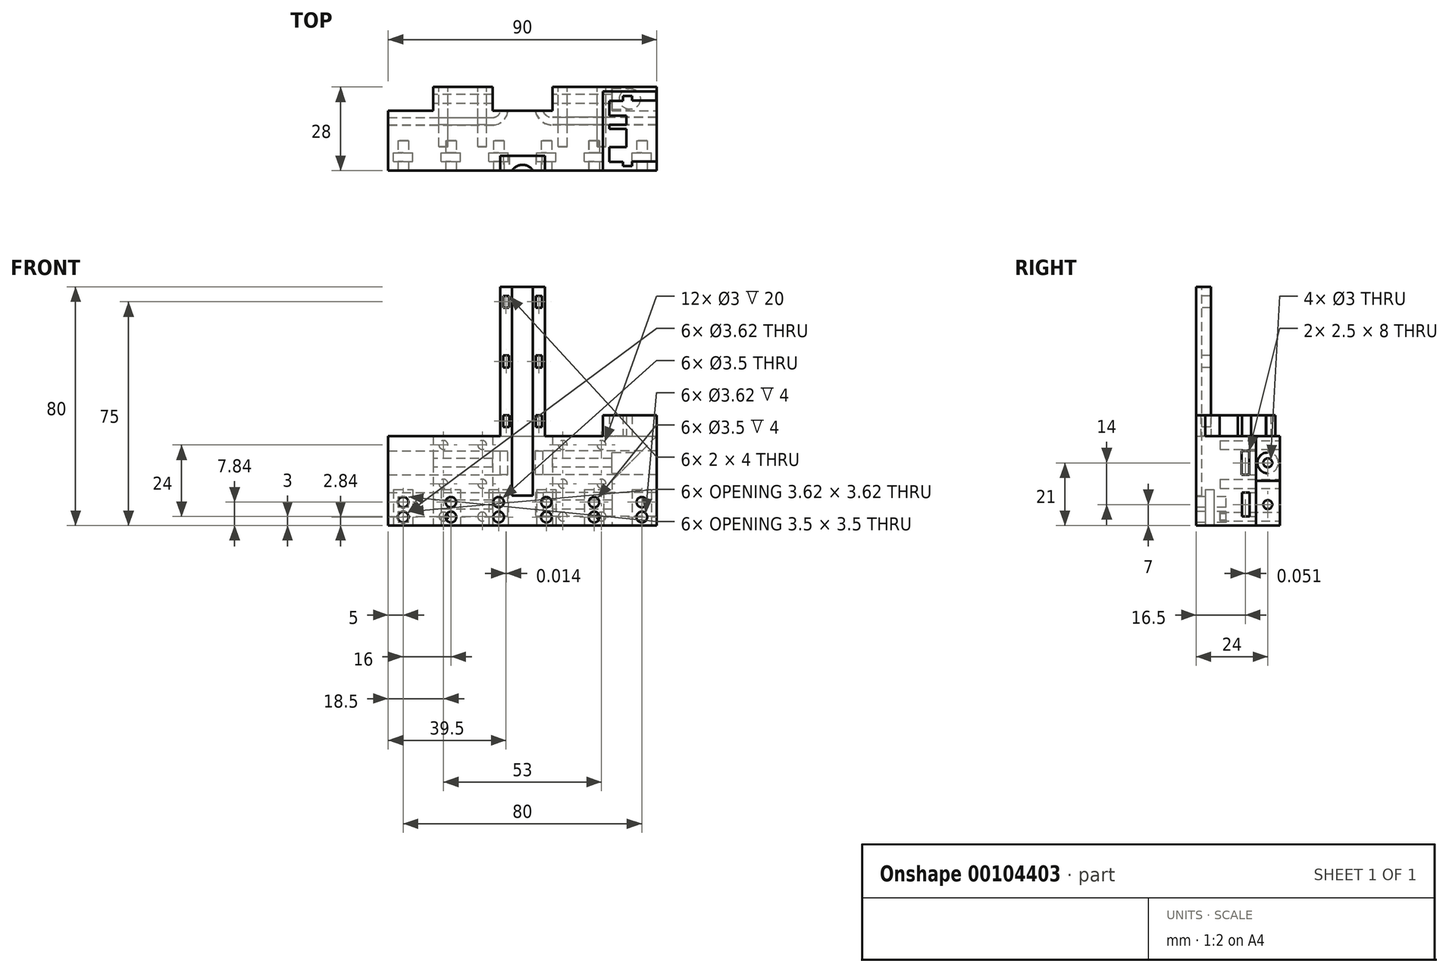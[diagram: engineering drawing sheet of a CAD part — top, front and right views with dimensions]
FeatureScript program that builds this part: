
annotation { "Feature Type Name" : "Feature", "Feature Type Description" : "" }
export const myFeature = defineFeature(function(context is Context, id is Id, definition is map)
    precondition{}
    {
        {
            var Q0;
            Q0=qCreatedBy(makeId("Top.planeOp"),FACE);
            var sketch = newSketch(context, id + "F0", { "sketchPlane" : qUnion([Q0])});
            skLineSegment(sketch, "E0.bottom", {"start": v(0, 0) * mm, "end": v(90, 0) * mm});
            skLineSegment(sketch, "E0.top", {"start": v(0, 20) * mm, "end": v(15, 20) * mm});
            skLineSegment(sketch, "E0.left", {"start": v(0, 0) * mm, "end": v(0, 20) * mm});
            skLineSegment(sketch, "E0.right", {"start": v(90, 0) * mm, "end": v(90, 20) * mm});
            skLineSegment(sketch, "E1.top", {"start": v(15, 28) * mm, "end": v(35, 28) * mm});
            skLineSegment(sketch, "E1.left", {"start": v(15, 20) * mm, "end": v(15, 28) * mm});
            skLineSegment(sketch, "E1.right", {"start": v(75, 20) * mm, "end": v(75, 28) * mm});
            skLineSegment(sketch, "E2.trimOffspring", {"start": v(75, 20) * mm, "end": v(90, 20) * mm});
            skLineSegment(sketch, "E3.top", {"start": v(35, 20) * mm, "end": v(55, 20) * mm});
            skLineSegment(sketch, "E3.left", {"start": v(35, 28) * mm, "end": v(35, 20) * mm});
            skLineSegment(sketch, "E3.right", {"start": v(55, 28) * mm, "end": v(55, 20) * mm});
            skLineSegment(sketch, "E4.trimOffspring", {"start": v(55, 28) * mm, "end": v(75, 28) * mm});
            skSolve(sketch);
        }
        {
            var Q0;
            Q0 = qSketchRegion(id + "F0", true);
            extrude(context, id + "F1", {"entities" : qUnion([Q0]), "depth" : 30 * mm});
        }
        {
            var Q0;
            Q0=makeQuery(id+"F1.opExtrude","CAP_FACE",FACE,{"disambiguationData":[OSD([sQuery(id+"F0.wireOp",EDGE,"E0.bottom"),sQuery(id+"F0.wireOp",EDGE,"E0.top"),sQuery(id+"F0.wireOp",EDGE,"E0.left"),sQuery(id+"F0.wireOp",EDGE,"E0.right"),sQuery(id+"F0.wireOp",EDGE,"E1.top"),sQuery(id+"F0.wireOp",EDGE,"E1.left"),sQuery(id+"F0.wireOp",EDGE,"E1.right"),sQuery(id+"F0.wireOp",EDGE,"E2.trimOffspring")])],"isStart":false});
            var sketch = newSketch(context, id + "F2", { "sketchPlane" : qUnion([Q0])});
            skLineSegment(sketch, "E5", {"start": v(0, 16.5) * mm, "end": v(35, 16.5) * mm});
            skArc(sketch, "E6", {"start": v(35, 16.5) * mm, "mid": v(37.78, 17.68) * mm, "end": v(38.86, 20.5) * mm});
            skLineSegment(sketch, "E7", {"start": v(90, 16.5) * mm, "end": v(55, 16.5) * mm});
            skArc(sketch, "E8", {"start": v(55, 16.5) * mm, "mid": v(51.9, 17.7) * mm, "end": v(50.38, 20.65) * mm});
            skSolve(sketch);
        }
        {
            var Q0;
            Q0=makeQuery(id+"F1.opExtrude","SWEPT_FACE",FACE,{"disambiguationData":[OSD([sQuery(id+"F0.wireOp",EDGE,"E0.left")])]});
            var sketch = newSketch(context, id + "F3", { "sketchPlane" : qUnion([Q0])});
            skLineSegment(sketch, "E9.bottom", {"start": v(-17.75, 25) * mm, "end": v(-15.25, 25) * mm});
            skLineSegment(sketch, "E9.top", {"start": v(-17.75, 17) * mm, "end": v(-15.25, 17) * mm});
            skLineSegment(sketch, "E9.left", {"start": v(-17.75, 25) * mm, "end": v(-17.75, 17) * mm});
            skLineSegment(sketch, "E9.right", {"start": v(-15.25, 25) * mm, "end": v(-15.25, 17) * mm});
            skLineSegment(sketch, "E10.bottom", {"start": v(-17.8, 11) * mm, "end": v(-15.3, 11) * mm});
            skLineSegment(sketch, "E10.top", {"start": v(-17.8, 3) * mm, "end": v(-15.3, 3) * mm});
            skLineSegment(sketch, "E10.left", {"start": v(-17.8, 11) * mm, "end": v(-17.8, 3) * mm});
            skLineSegment(sketch, "E10.right", {"start": v(-15.3, 11) * mm, "end": v(-15.3, 3) * mm});
            skSolve(sketch);
        }
        {
            var Q0;
            Q0 = qSketchRegion(id + "F3", true);
            var Q1;
            Q1=sQuery(id+"F2.wireOp",EDGE,"E5");
            var Q2;
            Q2=sQuery(id+"F2.wireOp",EDGE,"E6");
            sweep(context, id + "F4", {"operationType" : NewBodyOperationType.REMOVE, "profiles" : qUnion([Q0]), "path" : qUnion([Q1, Q2])});
        }
        {
            var Q0;
            Q0=makeQuery(id+"F1.opExtrude","SWEPT_FACE",FACE,{"disambiguationData":[OSD([sQuery(id+"F0.wireOp",EDGE,"E0.right")])]});
            var sketch = newSketch(context, id + "F5", { "sketchPlane" : qUnion([Q0])});
            skLineSegment(sketch, "E11.bottom", {"start": v(15.25, 25) * mm, "end": v(17.75, 25) * mm});
            skLineSegment(sketch, "E11.top", {"start": v(15.25, 17) * mm, "end": v(17.75, 17) * mm});
            skLineSegment(sketch, "E11.left", {"start": v(15.25, 25) * mm, "end": v(15.25, 17) * mm});
            skLineSegment(sketch, "E11.right", {"start": v(17.75, 25) * mm, "end": v(17.75, 17) * mm});
            skLineSegment(sketch, "E12.bottom", {"start": v(15.34, 11) * mm, "end": v(17.84, 11) * mm});
            skLineSegment(sketch, "E12.top", {"start": v(15.34, 3) * mm, "end": v(17.84, 3) * mm});
            skLineSegment(sketch, "E12.left", {"start": v(15.34, 11) * mm, "end": v(15.34, 3) * mm});
            skLineSegment(sketch, "E12.right", {"start": v(17.84, 11) * mm, "end": v(17.84, 3) * mm});
            skSolve(sketch);
        }
        {
            var Q0;
            Q0 = qSketchRegion(id + "F5", true);
            var Q1;
            Q1=sQuery(id+"F2.wireOp",EDGE,"E7");
            var Q2;
            Q2=sQuery(id+"F2.wireOp",EDGE,"E8");
            sweep(context, id + "F6", {"operationType" : NewBodyOperationType.REMOVE, "profiles" : qUnion([Q0]), "path" : qUnion([Q1, Q2])});
        }
        {
            var Q0;
            Q0=makeQuery(id+"F1.opExtrude","SWEPT_FACE",FACE,{"disambiguationData":[OSD([sQuery(id+"F0.wireOp",EDGE,"E1.left")])]});
            var sketch = newSketch(context, id + "F7", { "sketchPlane" : qUnion([Q0])});
            skCircle(sketch, "E13", {"center": v(-24, 21) * mm, "radius": 1.5 * mm});
            skCircle(sketch, "E14", {"center": v(-24, 7) * mm, "radius": 1.5 * mm});
            skSolve(sketch);
        }
        {
            var Q0;
            Q0=makeQuery(id+"F1.opExtrude","SWEPT_FACE",FACE,{"disambiguationData":[OSD([sQuery(id+"F0.wireOp",EDGE,"E0.bottom")])]});
            var sketch = newSketch(context, id + "F8", { "sketchPlane" : qUnion([Q0])});
            skCircle(sketch, "E15", {"center": v(5, 2.84) * mm, "radius": 1.81 * mm});
            skCircle(sketch, "E16", {"center": v(5, 7.84) * mm, "radius": 1.75 * mm});
            skCircle(sketch, "E17.1.0.0", {"center": v(21, 7.84) * mm, "radius": 1.75 * mm});
            skCircle(sketch, "E17.1.0.1", {"center": v(21, 2.84) * mm, "radius": 1.81 * mm});
            skCircle(sketch, "E17.2.0.0", {"center": v(37, 7.84) * mm, "radius": 1.75 * mm});
            skCircle(sketch, "E17.2.0.1", {"center": v(37, 2.84) * mm, "radius": 1.81 * mm});
            skCircle(sketch, "E17.3.0.0", {"center": v(53, 7.84) * mm, "radius": 1.75 * mm});
            skCircle(sketch, "E17.3.0.1", {"center": v(53, 2.84) * mm, "radius": 1.81 * mm});
            skCircle(sketch, "E17.4.0.0", {"center": v(69, 7.84) * mm, "radius": 1.75 * mm});
            skCircle(sketch, "E17.4.0.1", {"center": v(69, 2.84) * mm, "radius": 1.81 * mm});
            skCircle(sketch, "E17.5.0.0", {"center": v(85, 7.84) * mm, "radius": 1.75 * mm});
            skCircle(sketch, "E17.5.0.1", {"center": v(85, 2.84) * mm, "radius": 1.81 * mm});
            skLineSegment(sketch, "E17.direction1", {"start": v(5, 2.84) * mm, "end": v(21, 2.84) * mm, "construction": true});
            skSolve(sketch);
        }
        {
            var Q0;
            Q0=makeQuery(id+"F1.opExtrude","CAP_FACE",FACE,{"disambiguationData":[OSD([sQuery(id+"F0.wireOp",EDGE,"E0.bottom"),sQuery(id+"F0.wireOp",EDGE,"E0.top"),sQuery(id+"F0.wireOp",EDGE,"E0.left"),sQuery(id+"F0.wireOp",EDGE,"E0.right"),sQuery(id+"F0.wireOp",EDGE,"E1.top"),sQuery(id+"F0.wireOp",EDGE,"E1.left"),sQuery(id+"F0.wireOp",EDGE,"E1.right"),sQuery(id+"F0.wireOp",EDGE,"E2.trimOffspring"),sQuery(id+"F0.wireOp",EDGE,"E3.top"),sQuery(id+"F0.wireOp",EDGE,"E3.left"),sQuery(id+"F0.wireOp",EDGE,"E3.right"),sQuery(id+"F0.wireOp",EDGE,"E4.trimOffspring")])],"isStart":true});
            var sketch = newSketch(context, id + "F9", { "sketchPlane" : qUnion([Q0])});
            skLineSegment(sketch, "E18.bottom", {"start": v(1.75, -3) * mm, "end": v(8.25, -3) * mm});
            skLineSegment(sketch, "E18.top", {"start": v(1.75, -6) * mm, "end": v(8.25, -6) * mm});
            skLineSegment(sketch, "E18.left", {"start": v(1.75, -3) * mm, "end": v(1.75, -6) * mm});
            skLineSegment(sketch, "E18.right", {"start": v(8.25, -3) * mm, "end": v(8.25, -6) * mm});
            skLineSegment(sketch, "E19.1.0.0", {"start": v(17.75, -6) * mm, "end": v(24.25, -6) * mm});
            skLineSegment(sketch, "E19.1.0.1", {"start": v(24.25, -3) * mm, "end": v(24.25, -6) * mm});
            skLineSegment(sketch, "E19.1.0.2", {"start": v(17.75, -3) * mm, "end": v(24.25, -3) * mm});
            skLineSegment(sketch, "E19.1.0.3", {"start": v(17.75, -3) * mm, "end": v(17.75, -6) * mm});
            skLineSegment(sketch, "E19.2.0.0", {"start": v(33.75, -6) * mm, "end": v(40.25, -6) * mm});
            skLineSegment(sketch, "E19.2.0.1", {"start": v(40.25, -3) * mm, "end": v(40.25, -6) * mm});
            skLineSegment(sketch, "E19.2.0.2", {"start": v(33.75, -3) * mm, "end": v(40.25, -3) * mm});
            skLineSegment(sketch, "E19.2.0.3", {"start": v(33.75, -3) * mm, "end": v(33.75, -6) * mm});
            skLineSegment(sketch, "E19.3.0.0", {"start": v(49.75, -6) * mm, "end": v(56.25, -6) * mm});
            skLineSegment(sketch, "E19.3.0.1", {"start": v(56.25, -3) * mm, "end": v(56.25, -6) * mm});
            skLineSegment(sketch, "E19.3.0.2", {"start": v(49.75, -3) * mm, "end": v(56.25, -3) * mm});
            skLineSegment(sketch, "E19.3.0.3", {"start": v(49.75, -3) * mm, "end": v(49.75, -6) * mm});
            skLineSegment(sketch, "E19.4.0.0", {"start": v(65.75, -6) * mm, "end": v(72.25, -6) * mm});
            skLineSegment(sketch, "E19.4.0.1", {"start": v(72.25, -3) * mm, "end": v(72.25, -6) * mm});
            skLineSegment(sketch, "E19.4.0.2", {"start": v(65.75, -3) * mm, "end": v(72.25, -3) * mm});
            skLineSegment(sketch, "E19.4.0.3", {"start": v(65.75, -3) * mm, "end": v(65.75, -6) * mm});
            skLineSegment(sketch, "E19.5.0.0", {"start": v(81.75, -6) * mm, "end": v(88.25, -6) * mm});
            skLineSegment(sketch, "E19.5.0.1", {"start": v(88.25, -3) * mm, "end": v(88.25, -6) * mm});
            skLineSegment(sketch, "E19.5.0.2", {"start": v(81.75, -3) * mm, "end": v(88.25, -3) * mm});
            skLineSegment(sketch, "E19.5.0.3", {"start": v(81.75, -3) * mm, "end": v(81.75, -6) * mm});
            skLineSegment(sketch, "E19.direction1", {"start": v(8.25, -6) * mm, "end": v(24.25, -6) * mm, "construction": true});
            skSolve(sketch);
        }
        {
            var Q0;
            Q0 = qSketchRegion(id + "F8", true);
            extrude(context, id + "F10", {"entities" : qUnion([Q0]), "operationType" : NewBodyOperationType.REMOVE, "oppositeDirection" : true, "depth" : 10 * mm});
        }
        {
            var Q0;
            Q0 = qSketchRegion(id + "F9", true);
            extrude(context, id + "F11", {"entities" : qUnion([Q0]), "operationType" : NewBodyOperationType.REMOVE, "oppositeDirection" : true, "depth" : 12 * mm});
        }
        {
            var Q0;
            Q0=makeQuery(id+"F1.opExtrude","SWEPT_FACE",FACE,{"disambiguationData":[OSD([sQuery(id+"F0.wireOp",EDGE,"E4.trimOffspring")])]});
            var sketch = newSketch(context, id + "F12", { "sketchPlane" : qUnion([Q0])});
            skCircle(sketch, "E20", {"center": v(-71.5, 27) * mm, "radius": 1.5 * mm});
            skCircle(sketch, "E21", {"center": v(-58.5, 27) * mm, "radius": 1.5 * mm});
            skCircle(sketch, "E22", {"center": v(-71.5, 14) * mm, "radius": 1.5 * mm});
            skCircle(sketch, "E23", {"center": v(-58.5, 14) * mm, "radius": 1.5 * mm});
            skCircle(sketch, "E24", {"center": v(-71.5, 3) * mm, "radius": 1.5 * mm});
            skCircle(sketch, "E25", {"center": v(-58.5, 3) * mm, "radius": 1.5 * mm});
            skLineSegment(sketch, "E26", {"start": v(-45, -4.16) * mm, "end": v(-45, 34.08) * mm, "construction": true});
            skCircle(sketch, "E27.MirrorC", {"center": v(-31.5, 3) * mm, "radius": 1.5 * mm});
            skCircle(sketch, "E28.MirrorC", {"center": v(-18.5, 3) * mm, "radius": 1.5 * mm});
            skCircle(sketch, "E29.MirrorC", {"center": v(-18.5, 14) * mm, "radius": 1.5 * mm});
            skCircle(sketch, "E30.MirrorC", {"center": v(-31.5, 14) * mm, "radius": 1.5 * mm});
            skCircle(sketch, "E31.MirrorC", {"center": v(-31.5, 27) * mm, "radius": 1.5 * mm});
            skCircle(sketch, "E32.MirrorC", {"center": v(-18.5, 27) * mm, "radius": 1.5 * mm});
            skSolve(sketch);
        }
        {
            var Q0;
            Q0 = qSketchRegion(id + "F12", true);
            extrude(context, id + "F13", {"entities" : qUnion([Q0]), "operationType" : NewBodyOperationType.REMOVE, "oppositeDirection" : true, "depth" : 20 * mm});
        }
        {
            var Q0;
            Q0=makeQuery(id+"F1.opExtrude","CAP_FACE",FACE,{"disambiguationData":[OSD([sQuery(id+"F0.wireOp",EDGE,"E0.bottom"),sQuery(id+"F0.wireOp",EDGE,"E0.top"),sQuery(id+"F0.wireOp",EDGE,"E0.left"),sQuery(id+"F0.wireOp",EDGE,"E0.right"),sQuery(id+"F0.wireOp",EDGE,"E1.top"),sQuery(id+"F0.wireOp",EDGE,"E1.left"),sQuery(id+"F0.wireOp",EDGE,"E1.right"),sQuery(id+"F0.wireOp",EDGE,"E2.trimOffspring"),sQuery(id+"F0.wireOp",EDGE,"E3.top"),sQuery(id+"F0.wireOp",EDGE,"E3.left"),sQuery(id+"F0.wireOp",EDGE,"E3.right"),sQuery(id+"F0.wireOp",EDGE,"E4.trimOffspring")])],"isStart":false});
            var sketch = newSketch(context, id + "F14", { "sketchPlane" : qUnion([Q0])});
            skLineSegment(sketch, "E33.bottom", {"start": v(37.5, 0) * mm, "end": v(52.5, 0) * mm});
            skLineSegment(sketch, "E33.top", {"start": v(37.5, 5) * mm, "end": v(52.5, 5) * mm});
            skLineSegment(sketch, "E33.left", {"start": v(37.5, 0) * mm, "end": v(37.5, 5) * mm});
            skLineSegment(sketch, "E33.right", {"start": v(52.5, 0) * mm, "end": v(52.5, 5) * mm});
            skSolve(sketch);
        }
        {
            var Q0;
            Q0 = qSketchRegion(id + "F14", true);
            extrude(context, id + "F15", {"entities" : qUnion([Q0]), "operationType" : NewBodyOperationType.ADD, "depth" : 50 * mm});
        }
        {
            var Q0;
            Q0=makeQuery(id+"F15.opExtrude","CAP_FACE",FACE,{"disambiguationData":[OSD([sQuery(id+"F14.wireOp",EDGE,"E33.bottom"),sQuery(id+"F14.wireOp",EDGE,"E33.top"),sQuery(id+"F14.wireOp",EDGE,"E33.left"),sQuery(id+"F14.wireOp",EDGE,"E33.right")])],"isStart":false});
            var sketch = newSketch(context, id + "F16", { "sketchPlane" : qUnion([Q0])});
            skArc(sketch, "E34", {"start": v(48.5, 0) * mm, "mid": v(45, 1.9) * mm, "end": v(41.5, 0) * mm});
            skLineSegment(sketch, "E35", {"start": v(41.5, 0) * mm, "end": v(48.5, 0) * mm});
            skSolve(sketch);
        }
        {
            var Q0;
            Q0 = qSketchRegion(id + "F16", true);
            extrude(context, id + "F17", {"entities" : qUnion([Q0]), "operationType" : NewBodyOperationType.REMOVE, "oppositeDirection" : true, "depth" : 70 * mm});
        }
        {
            var Q0;
            Q0=makeQuery(id+"F15.boolean.opBoolean","MERGE",FACE,{"derivedFrom":[makeQuery(id+"F1.opExtrude","SWEPT_FACE",FACE,{"disambiguationData":[OSD([sQuery(id+"F0.wireOp",EDGE,"E0.bottom")])]}),makeQuery(id+"F15.opExtrude","SWEPT_FACE",FACE,{"disambiguationData":[OSD([sQuery(id+"F14.wireOp",EDGE,"E33.bottom")])]})]});
            var sketch = newSketch(context, id + "F18", { "sketchPlane" : qUnion([Q0])});
            skLineSegment(sketch, "E36.bottom", {"start": v(38.5, 77) * mm, "end": v(40.5, 77) * mm});
            skLineSegment(sketch, "E36.top", {"start": v(38.5, 73) * mm, "end": v(40.5, 73) * mm});
            skLineSegment(sketch, "E36.left", {"start": v(38.5, 77) * mm, "end": v(38.5, 73) * mm});
            skLineSegment(sketch, "E36.right", {"start": v(40.5, 77) * mm, "end": v(40.5, 73) * mm});
            skLineSegment(sketch, "E37.1.0.0", {"start": v(38.51, 53) * mm, "end": v(40.51, 53) * mm});
            skLineSegment(sketch, "E37.1.0.1", {"start": v(40.51, 57) * mm, "end": v(40.51, 53) * mm});
            skLineSegment(sketch, "E37.1.0.2", {"start": v(38.51, 57) * mm, "end": v(38.51, 53) * mm});
            skLineSegment(sketch, "E37.1.0.3", {"start": v(38.51, 57) * mm, "end": v(40.51, 57) * mm});
            skLineSegment(sketch, "E37.2.0.0", {"start": v(38.53, 33) * mm, "end": v(40.53, 33) * mm});
            skLineSegment(sketch, "E37.2.0.1", {"start": v(40.53, 37) * mm, "end": v(40.53, 33) * mm});
            skLineSegment(sketch, "E37.2.0.2", {"start": v(38.53, 37) * mm, "end": v(38.53, 33) * mm});
            skLineSegment(sketch, "E37.2.0.3", {"start": v(38.53, 37) * mm, "end": v(40.53, 37) * mm});
            skLineSegment(sketch, "E37.direction1", {"start": v(38.5, 73) * mm, "end": v(38.51, 53) * mm, "construction": true});
            skLineSegment(sketch, "E38", {"start": v(45, 83.56) * mm, "end": v(45, 31.13) * mm, "construction": true});
            skLineSegment(sketch, "E39.MirrorCS", {"start": v(49.5, 77) * mm, "end": v(49.5, 73) * mm});
            skLineSegment(sketch, "E40.MirrorCS", {"start": v(51.5, 77) * mm, "end": v(49.5, 77) * mm});
            skLineSegment(sketch, "E41.MirrorCS", {"start": v(51.5, 77) * mm, "end": v(51.5, 73) * mm});
            skLineSegment(sketch, "E42.MirrorCS", {"start": v(51.5, 73) * mm, "end": v(49.5, 73) * mm});
            skLineSegment(sketch, "E43.MirrorCS", {"start": v(51.49, 57) * mm, "end": v(49.49, 57) * mm});
            skLineSegment(sketch, "E44.MirrorCS", {"start": v(49.49, 57) * mm, "end": v(49.49, 53) * mm});
            skLineSegment(sketch, "E45.MirrorCS", {"start": v(51.49, 53) * mm, "end": v(49.49, 53) * mm});
            skLineSegment(sketch, "E46.MirrorCS", {"start": v(51.49, 57) * mm, "end": v(51.49, 53) * mm});
            skLineSegment(sketch, "E47.MirrorCS", {"start": v(51.47, 37) * mm, "end": v(49.47, 37) * mm});
            skLineSegment(sketch, "E48.MirrorCS", {"start": v(49.47, 37) * mm, "end": v(49.47, 33) * mm});
            skLineSegment(sketch, "E49.MirrorCS", {"start": v(51.47, 33) * mm, "end": v(49.47, 33) * mm});
            skLineSegment(sketch, "E50.MirrorCS", {"start": v(51.47, 37) * mm, "end": v(51.47, 33) * mm});
            skSolve(sketch);
        }
        {
            var Q0;
            Q0 = qSketchRegion(id + "F18", true);
            extrude(context, id + "F19", {"entities" : qUnion([Q0]), "operationType" : NewBodyOperationType.REMOVE, "endBound" : BoundingType.THROUGH_ALL, "oppositeDirection" : true, "depth" : 25 * mm});
        }
        {
            var Q0;
            Q0=makeQuery(id+"F1.opExtrude","CAP_FACE",FACE,{"disambiguationData":[OSD([sQuery(id+"F0.wireOp",EDGE,"E0.bottom"),sQuery(id+"F0.wireOp",EDGE,"E0.top"),sQuery(id+"F0.wireOp",EDGE,"E0.left"),sQuery(id+"F0.wireOp",EDGE,"E0.right"),sQuery(id+"F0.wireOp",EDGE,"E1.top"),sQuery(id+"F0.wireOp",EDGE,"E1.left"),sQuery(id+"F0.wireOp",EDGE,"E1.right"),sQuery(id+"F0.wireOp",EDGE,"E2.trimOffspring"),sQuery(id+"F0.wireOp",EDGE,"E3.top"),sQuery(id+"F0.wireOp",EDGE,"E3.left"),sQuery(id+"F0.wireOp",EDGE,"E3.right"),sQuery(id+"F0.wireOp",EDGE,"E4.trimOffspring")])],"isStart":false});
            var sketch = newSketch(context, id + "F20", { "sketchPlane" : qUnion([Q0])});
            skLineSegment(sketch, "E51.bottom", {"start": v(81.7, 23.5) * mm, "end": v(89.8, 23.5) * mm});
            skLineSegment(sketch, "E51.top", {"start": v(81.7, 3) * mm, "end": v(90, 3) * mm});
            skLineSegment(sketch, "E51.left", {"start": v(79.8, 18.39) * mm, "end": v(79.8, 15.38) * mm});
            skLineSegment(sketch, "E52", {"start": v(90, 0) * mm, "end": v(72, 0) * mm});
            skLineSegment(sketch, "E53", {"start": v(72, 26.5) * mm, "end": v(89.8, 26.5) * mm});
            skLineSegment(sketch, "E54", {"start": v(89.8, 26.5) * mm, "end": v(89.8, 23.5) * mm});
            skLineSegment(sketch, "E55", {"start": v(90, 3) * mm, "end": v(90, 0) * mm});
            skLineSegment(sketch, "E56.bottom", {"start": v(78.73, 23.39) * mm, "end": v(74.09, 23.39) * mm});
            skLineSegment(sketch, "E56.top", {"start": v(79.8, 18.39) * mm, "end": v(74.09, 18.39) * mm});
            skLineSegment(sketch, "E56.right", {"start": v(74.09, 23.39) * mm, "end": v(74.09, 18.39) * mm});
            skLineSegment(sketch, "E57.bottom", {"start": v(78.73, 2.89) * mm, "end": v(74.09, 2.89) * mm});
            skLineSegment(sketch, "E57.top", {"start": v(79.8, 7.89) * mm, "end": v(74.09, 7.89) * mm});
            skLineSegment(sketch, "E57.right", {"start": v(74.09, 2.89) * mm, "end": v(74.09, 7.89) * mm});
            skLineSegment(sketch, "E58.bottom", {"start": v(79.8, 15.38) * mm, "end": v(74.09, 15.38) * mm});
            skLineSegment(sketch, "E58.top", {"start": v(79.8, 13.93) * mm, "end": v(74.09, 13.93) * mm});
            skLineSegment(sketch, "E58.right", {"start": v(74.09, 15.38) * mm, "end": v(74.09, 13.93) * mm});
            skLineSegment(sketch, "E59.trimOffspring", {"start": v(79.8, 13.93) * mm, "end": v(79.8, 7.89) * mm});
            skLineSegment(sketch, "E60.top", {"start": v(78.73, 24.96) * mm, "end": v(81.7, 24.96) * mm});
            skLineSegment(sketch, "E60.left", {"start": v(78.73, 23.39) * mm, "end": v(78.73, 24.96) * mm});
            skLineSegment(sketch, "E60.right", {"start": v(81.7, 23.5) * mm, "end": v(81.7, 24.96) * mm});
            skLineSegment(sketch, "E61.top", {"start": v(78.73, 1.5) * mm, "end": v(81.7, 1.5) * mm});
            skLineSegment(sketch, "E61.left", {"start": v(78.73, 2.89) * mm, "end": v(78.73, 1.5) * mm});
            skLineSegment(sketch, "E61.right", {"start": v(81.7, 3) * mm, "end": v(81.7, 1.5) * mm});
            skLineSegment(sketch, "E62", {"start": v(72, 26.5) * mm, "end": v(72, 0) * mm});
            skSolve(sketch);
        }
        {
            var Q0;
            Q0=makeQuery(id+"F1.opExtrude","SWEPT_FACE",FACE,{"disambiguationData":[OSD([sQuery(id+"F0.wireOp",EDGE,"E2.trimOffspring")])]});
            var sketch = newSketch(context, id + "F21", { "sketchPlane" : qUnion([Q0])});
            skLineSegment(sketch, "E63", {"start": v(-90, 30) * mm, "end": v(-75, 30) * mm});
            skLineSegment(sketch, "E64", {"start": v(-75, 30) * mm, "end": v(-75, 15) * mm});
            skLineSegment(sketch, "E65", {"start": v(-75, 15) * mm, "end": v(-90, 30) * mm});
            skSolve(sketch);
        }
        {
            var Q0;
            Q0 = qSketchRegion(id + "F21", true);
            var Q1;
            Q1=makeQuery(id+"F1.opExtrude","SWEPT_FACE",FACE,{"disambiguationData":[OSD([sQuery(id+"F0.wireOp",EDGE,"E4.trimOffspring")])]});
            extrude(context, id + "F22", {"entities" : qUnion([Q0]), "operationType" : NewBodyOperationType.ADD, "endBoundEntityFace" : qUnion([Q1]), "depth" : 8 * mm});
        }
        {
            var Q0;
            Q0 = qSketchRegion(id + "F7", true);
            extrude(context, id + "F23", {"entities" : qUnion([Q0]), "operationType" : NewBodyOperationType.REMOVE, "endBound" : BoundingType.THROUGH_ALL, "oppositeDirection" : true, "depth" : 25 * mm});
        }
        {
            var Q0;
            Q0=makeQuery(id+"F1.opExtrude","SWEPT_FACE",FACE,{"disambiguationData":[OSD([sQuery(id+"F0.wireOp",EDGE,"E0.right")])]});
            var sketch = newSketch(context, id + "F24", { "sketchPlane" : qUnion([Q0])});
            skCircle(sketch, "E66", {"center": v(24.03, 21) * mm, "radius": 3.5 * mm});
            skSolve(sketch);
        }
        {
            var Q0;
            Q0 = qSketchRegion(id + "F24", true);
            extrude(context, id + "F25", {"entities" : qUnion([Q0]), "operationType" : NewBodyOperationType.REMOVE, "oppositeDirection" : true, "depth" : 15 * mm});
        }
        {
            var Q0;
            Q0 = qSketchRegion(id + "F20", true);
            extrude(context, id + "F26", {"entities" : qUnion([Q0]), "operationType" : NewBodyOperationType.ADD, "depth" : 7 * mm});
        }
    });
